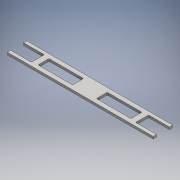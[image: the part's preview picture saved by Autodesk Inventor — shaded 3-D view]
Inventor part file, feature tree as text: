
AUTODESK INVENTOR PART (.ipt)
format: ipt  version: 2016 (Build 200138000, 138)  size: 134,656 bytes
history: native  units: mm
features: extrude x1, sketch x1
ambient origin geometry x8: Origin, YZ Plane, XZ Plane, XY Plane, X Axis, Y Axis, Z Axis, Center Point
bodies: Solid1 (feature_tree)
feature tree (2):
  extrude  "Extrusion1"  Depth=9.525mm TaperAngle=0.0deg
  sketch  "Sketch1"  dims[d0=135.4582mm d1=43.104285mm d2=16.546659mm d3=16.529mm d4=21.585333mm d5=92.185791mm d6=9.525mm d7=0.0mm]
